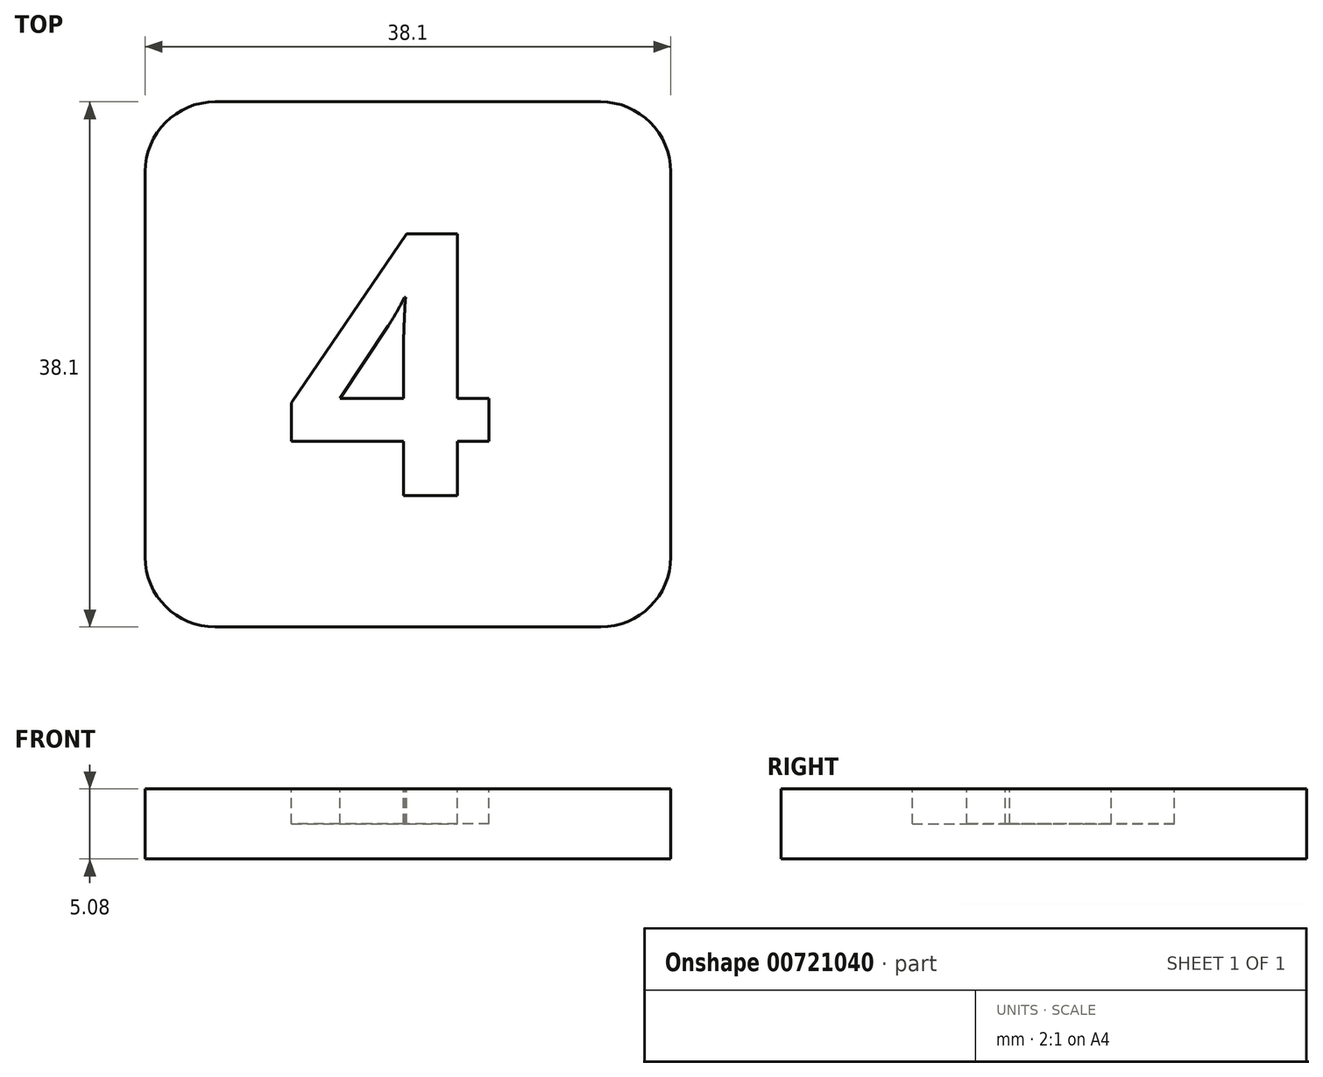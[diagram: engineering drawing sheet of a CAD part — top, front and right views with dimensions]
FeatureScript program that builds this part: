
annotation { "Feature Type Name" : "Feature", "Feature Type Description" : "" }
export const myFeature = defineFeature(function(context is Context, id is Id, definition is map)
    precondition{}
    {
        {
            var Q0;
            Q0=qCreatedBy(makeId("Top.planeOp"),FACE);
            var sketch = newSketch(context, id + "F0", { "sketchPlane" : qUnion([Q0])});
            skLineSegment(sketch, "E0.bottom", {"start": v(-19.05, 19.05) * mm, "end": v(19.05, 19.05) * mm});
            skLineSegment(sketch, "E0.top", {"start": v(-19.05, -19.05) * mm, "end": v(19.05, -19.05) * mm});
            skLineSegment(sketch, "E0.left", {"start": v(-19.05, 19.05) * mm, "end": v(-19.05, -19.05) * mm});
            skLineSegment(sketch, "E0.right", {"start": v(19.05, 19.05) * mm, "end": v(19.05, -19.05) * mm});
            skPoint(sketch, "E0.middle", {"position": v(0, 0) * mm});
            skSolve(sketch);
        }
        {
            var Q0;
            Q0=qSketchRegion(id+"F0",true);
            extrude(context, id + "F1", {"entities" : qUnion([Q0]), "depth" : 5.08 * mm, "offsetDistance" : 25.4 * mm});
        }
        {
            var Q0;
            Q0=makeQuery(id+"F1.opExtrude","CAP_FACE",FACE,{"disambiguationData":[OSD([sQuery(id+"F0.wireOp",EDGE,"E0.bottom"),sQuery(id+"F0.wireOp",EDGE,"E0.top"),sQuery(id+"F0.wireOp",EDGE,"E0.left"),sQuery(id+"F0.wireOp",EDGE,"E0.right")])],"isStart":false});
            var sketch = newSketch(context, id + "F2", { "sketchPlane" : qUnion([Q0])});
            skText(sketch, "E1", { "text": "4", "fontName": "OpenSans-Bold.ttf"});
            const initialGuessF2  = {"E1": [-0.0089, -0.00953, 1, 0, 0.01917]};
            skSetInitialGuess(sketch, initialGuessF2);
            skSolve(sketch);
        }
        {
            var Q0;
            Q0=qSketchRegion(id+"F2",true);
            extrude(context, id + "F3", {"entities" : qUnion([Q0]), "operationType" : NewBodyOperationType.REMOVE, "oppositeDirection" : true, "depth" : 2.54 * mm, "offsetDistance" : 25.4 * mm});
        }
        {
            var Q0;
            Q0=makeQuery(id+"F1.opExtrude","SWEPT_EDGE",EDGE,{"disambiguationData":[OSD([sQuery(id+"F0.wireOp",EDGE,"E0.top"),sQuery(id+"F0.wireOp",EDGE,"E0.left")])]});
            var Q1;
            Q1=makeQuery(id+"F1.opExtrude","SWEPT_EDGE",EDGE,{"disambiguationData":[OSD([sQuery(id+"F0.wireOp",EDGE,"E0.top"),sQuery(id+"F0.wireOp",EDGE,"E0.right")])]});
            var Q2;
            Q2=makeQuery(id+"F1.opExtrude","SWEPT_EDGE",EDGE,{"disambiguationData":[OSD([sQuery(id+"F0.wireOp",EDGE,"E0.bottom"),sQuery(id+"F0.wireOp",EDGE,"E0.right")])]});
            var Q3;
            Q3=makeQuery(id+"F1.opExtrude","SWEPT_EDGE",EDGE,{"disambiguationData":[OSD([sQuery(id+"F0.wireOp",EDGE,"E0.bottom"),sQuery(id+"F0.wireOp",EDGE,"E0.left")])]});
            fillet(context, id + "F4", {"entities" : qUnion([Q0, Q1, Q2, Q3]), "radius" : 5.08 * mm, "tangentPropagation" : true, "allowEdgeOverflow" : false});
        }
    });
